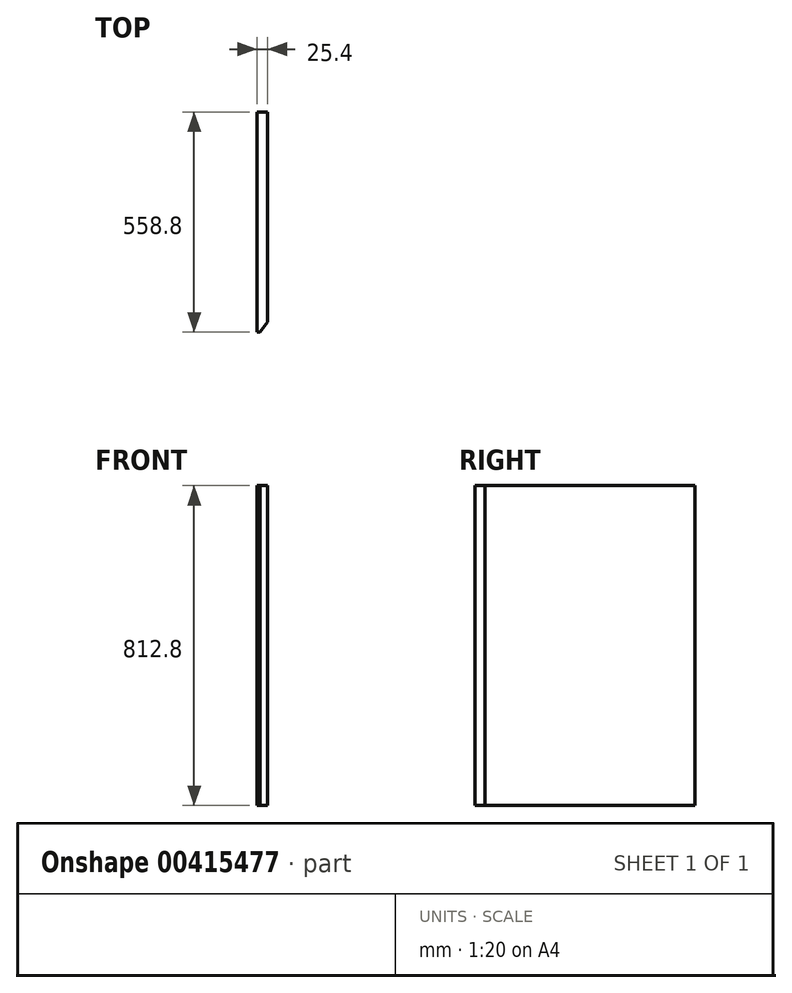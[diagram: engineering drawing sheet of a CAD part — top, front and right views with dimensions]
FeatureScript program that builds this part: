
annotation { "Feature Type Name" : "Feature", "Feature Type Description" : "" }
export const myFeature = defineFeature(function(context is Context, id is Id, definition is map)
    precondition{}
    {
        {
            var Q0;
            Q0=qCreatedBy(makeId("Right.planeOp"),FACE);
            var sketch = newSketch(context, id + "F0", { "sketchPlane" : qUnion([Q0])});
            skLineSegment(sketch, "E0.bottom", {"start": v(-279.4, -406.4) * mm, "end": v(279.4, -406.4) * mm});
            skLineSegment(sketch, "E0.top", {"start": v(-279.4, 406.4) * mm, "end": v(279.4, 406.4) * mm});
            skLineSegment(sketch, "E0.left", {"start": v(-279.4, -406.4) * mm, "end": v(-279.4, 406.4) * mm});
            skLineSegment(sketch, "E0.right", {"start": v(279.4, -406.4) * mm, "end": v(279.4, 406.4) * mm});
            skPoint(sketch, "E0.middle", {"position": v(0, 0) * mm});
            skSolve(sketch);
        }
        {
            var Q0;
            Q0=makeQuery(id+"F0.imprint","IMPRINT",FACE,{"disambiguationData":[TD([[makeQuery(id+"F0.imprint","IMPRINT",EDGE,{"derivedFrom":sQuery(id+"F0.wireOp",EDGE,"E0.bottom")}),1.0]])]});
            extrude(context, id + "F1", {"entities" : qUnion([Q0]), "depth" : 25.4 * mm});
        }
        {
            var Q0;
            Q0=makeQuery(id+"F1.opExtrude","CAP_EDGE",EDGE,{"disambiguationData":[OSD([sQuery(id+"F0.wireOp",EDGE,"E0.left")])],"isStart":false});
            chamfer(context, id + "F2", {"entities" : qUnion([Q0]), "chamferType" : ChamferType.TWO_OFFSETS, "width1" : 19.05 * mm, "oppositeDirection" : false, "width2" : 25.4 * mm, "tangentPropagation" : true});
        }
    });
